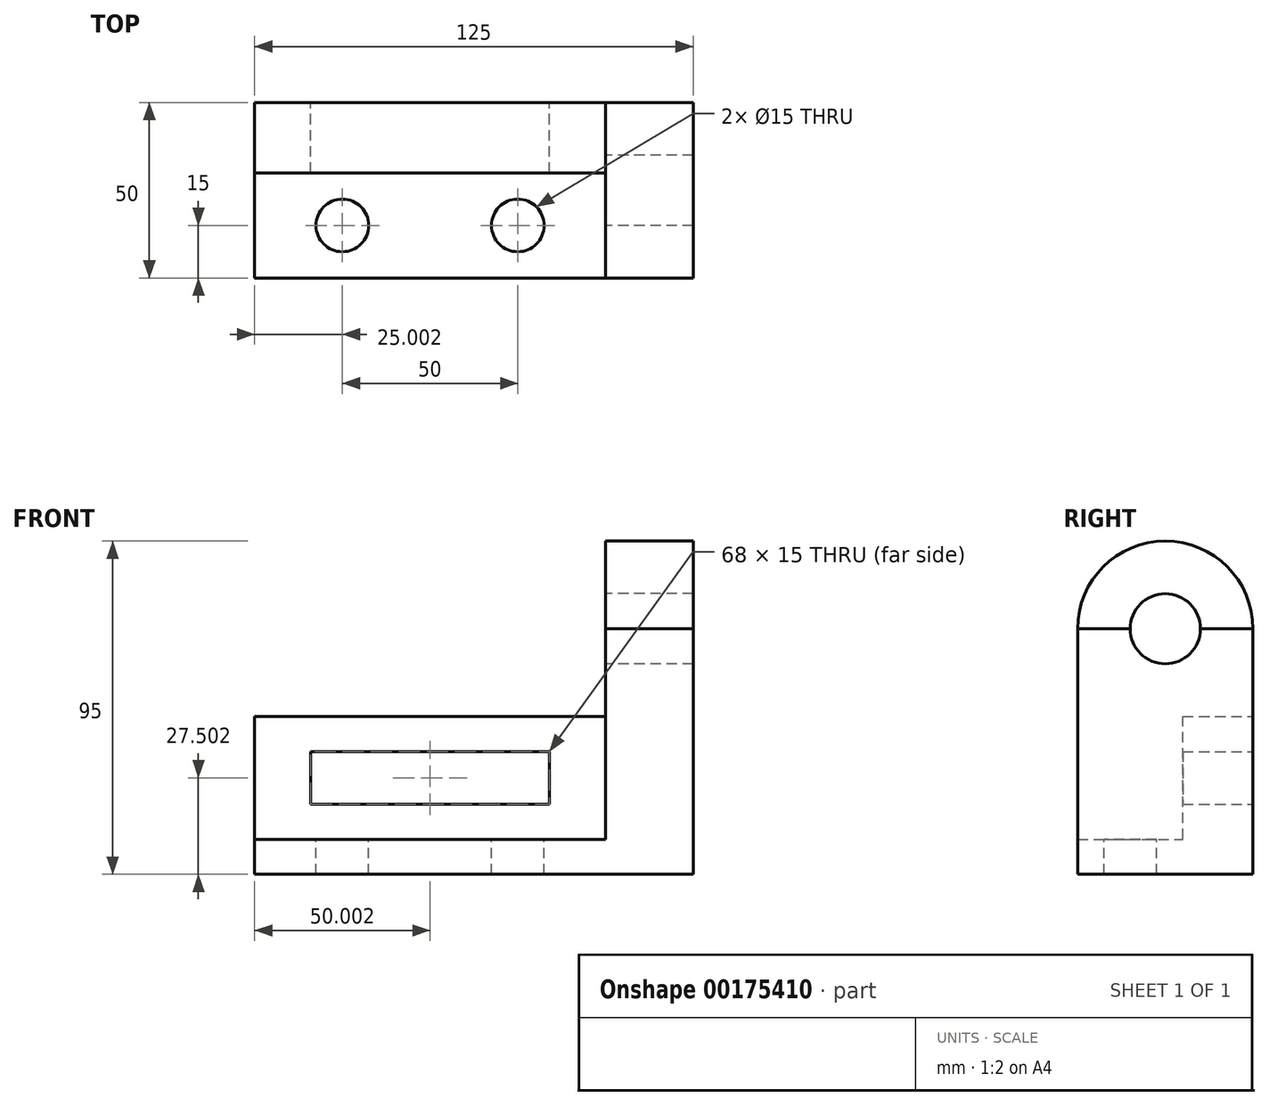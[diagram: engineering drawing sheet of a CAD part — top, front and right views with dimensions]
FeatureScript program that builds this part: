
annotation { "Feature Type Name" : "Feature", "Feature Type Description" : "" }
export const myFeature = defineFeature(function(context is Context, id is Id, definition is map)
    precondition{}
    {
        {
            var Q0;
            Q0=qCreatedBy(makeId("Front.planeOp"),FACE);
            var sketch = newSketch(context, id + "F0", { "sketchPlane" : qUnion([Q0])});
            skLineSegment(sketch, "E0.right", {"start": v(-50, 4.52) * mm, "end": v(-50, -5.48) * mm});
            skPoint(sketch, "E0.middle", {"position": v(0, 0) * mm});
            skLineSegment(sketch, "E1", {"start": v(-50, -5.48) * mm, "end": v(75, -5.48) * mm});
            skLineSegment(sketch, "E2", {"start": v(75, -5.48) * mm, "end": v(75, 64.52) * mm});
            skLineSegment(sketch, "E3", {"start": v(-50, 4.52) * mm, "end": v(50, 4.52) * mm});
            skLineSegment(sketch, "E4", {"start": v(50, 4.52) * mm, "end": v(50, 64.52) * mm});
            skLineSegment(sketch, "E5", {"start": v(-50, 4.52) * mm, "end": v(-50, 39.52) * mm});
            skLineSegment(sketch, "E6", {"start": v(-50, 39.52) * mm, "end": v(50, 39.52) * mm});
            skLineSegment(sketch, "E7", {"start": v(-34, 29.52) * mm, "end": v(34, 29.52) * mm});
            skLineSegment(sketch, "E8", {"start": v(-34, 29.52) * mm, "end": v(-34, 14.52) * mm});
            skLineSegment(sketch, "E9", {"start": v(34, 29.52) * mm, "end": v(34, 14.52) * mm});
            skLineSegment(sketch, "E10", {"start": v(-34, 14.52) * mm, "end": v(34, 14.52) * mm});
            skLineSegment(sketch, "E11", {"start": v(50, 64.52) * mm, "end": v(75, 64.52) * mm});
            skSolve(sketch);
        }
        {
            var Q0;
            Q0 = qSketchRegion(id + "F0", true);
            extrude(context, id + "F1", {"entities" : qUnion([Q0]), "depth" : 50 * mm});
        }
        {
            var Q0;
            Q0=makeQuery(id+"F1.opExtrude","SWEPT_FACE",FACE,{"disambiguationData":[OSD([sQuery(id+"F0.wireOp",EDGE,"E6")])]});
            var sketch = newSketch(context, id + "F2", { "sketchPlane" : qUnion([Q0])});
            skLineSegment(sketch, "E12", {"start": v(-50, 0) * mm, "end": v(-50, -20) * mm});
            skLineSegment(sketch, "E13", {"start": v(-50, -20) * mm, "end": v(50, -20) * mm});
            skLineSegment(sketch, "E14", {"start": v(50, -20) * mm, "end": v(50, 0) * mm});
            skLineSegment(sketch, "E15", {"start": v(50, 0) * mm, "end": v(-50, 0) * mm});
            skSolve(sketch);
        }
        {
            var Q0;
            {var subQ0=sQuery(id+"F2.wireOp",EDGE,"E13");Q0=makeQuery(id+"F2.imprint","IMPRINT",FACE,{"disambiguationData":[TD([[makeQuery(id+"F2.imprint","IMPRINT",EDGE,{"derivedFrom":subQ0}),-1.0]])]});}
            var sketch = newSketch(context, id + "F3", { "sketchPlane" : qUnion([Q0])});
            skSolve(sketch);
        }
        {
            var Q0;
            Q0 = qSketchRegion(id + "F3", true);
            var Q1;
            {var subQ0=sQuery(id+"F2.wireOp",EDGE,"E13");Q1=makeQuery(id+"F2.imprint","IMPRINT",FACE,{"disambiguationData":[TD([[makeQuery(id+"F2.imprint","IMPRINT",EDGE,{"derivedFrom":subQ0}),-1.0]])]});}
            extrude(context, id + "F4", {"entities" : qUnion([Q0, Q1]), "operationType" : NewBodyOperationType.REMOVE, "oppositeDirection" : true, "depth" : 35 * mm});
        }
        {
            var Q0;
            Q0=makeQuery(id+"F4.boolean.opBoolean","COPY",FACE,{"derivedFrom":makeQuery(id+"F4.opExtrude","CAP_FACE",FACE,{"disambiguationData":[OSD([sQuery(id+"F0.wireOp",EDGE,"E4"),sQuery(id+"F0.wireOp",EDGE,"E5"),sQuery(id+"F0.wireOp",EDGE,"E6"),sQuery(id+"F2.wireOp",EDGE,"E13")])],"isStart":false})});
            var sketch = newSketch(context, id + "F5", { "sketchPlane" : qUnion([Q0])});
            skLineSegment(sketch, "E16", {"start": v(-25, -20) * mm, "end": v(-50, -20) * mm});
            skLineSegment(sketch, "E17", {"start": v(25, -20) * mm, "end": v(50, -20) * mm});
            skLineSegment(sketch, "E18", {"start": v(50, -20) * mm, "end": v(50, -35) * mm});
            skLineSegment(sketch, "E19", {"start": v(50, -35) * mm, "end": v(50, -20) * mm});
            skCircle(sketch, "E20", {"center": v(-25, -35) * mm, "radius": 7.5 * mm});
            skCircle(sketch, "E21", {"center": v(25, -35) * mm, "radius": 7.5 * mm});
            skSolve(sketch);
        }
        {
            var Q0;
            Q0 = qSketchRegion(id + "F5", true);
            extrude(context, id + "F6", {"entities" : qUnion([Q0]), "operationType" : NewBodyOperationType.REMOVE, "oppositeDirection" : true, "depth" : 2540 * mm});
        }
        {
            var Q0;
            Q0=makeQuery(id+"F1.opExtrude","SWEPT_FACE",FACE,{"disambiguationData":[OSD([sQuery(id+"F0.wireOp",EDGE,"E2")])]});
            var sketch = newSketch(context, id + "F7", { "sketchPlane" : qUnion([Q0])});
            skArc(sketch, "E22", {"start": v(0, 64.52) * mm, "mid": v(-25, 89.52) * mm, "end": v(-50, 64.52) * mm});
            skSolve(sketch);
        }
        {
            var Q0;
            Q0=makeQuery(id+"F7.imprint","IMPRINT",FACE,{"disambiguationData":[TD([[makeQuery(id+"F7.imprint","IMPRINT",EDGE,{"derivedFrom":sQuery(id+"F7.wireOp",EDGE,"E22")}),1.0]])]});
            extrude(context, id + "F8", {"entities" : qUnion([Q0]), "oppositeDirection" : true, "depth" : 25 * mm});
        }
        {
            var Q0;
            {var subQ0=sQuery(id+"F0.wireOp",EDGE,"E4");Q0=makeQuery(id+"F4.boolean.opBoolean","MERGE",FACE,{"derivedFrom":[makeQuery(id+"F1.opExtrude","SWEPT_FACE",FACE,{"disambiguationData":[OSD([subQ0])]}),makeQuery(id+"F4.opExtrude","SWEPT_FACE",FACE,{"disambiguationData":[OSD([subQ0,sQuery(id+"F0.wireOp",EDGE,"E6")])]})]});}
            var sketch = newSketch(context, id + "F9", { "sketchPlane" : qUnion([Q0])});
            skCircle(sketch, "E23", {"center": v(25, 64.52) * mm, "radius": 10 * mm});
            skSolve(sketch);
        }
        {
            var Q0;
            {var subQ0=sQuery(id+"F9.wireOp",EDGE,"E23");var subQ1=makeQuery(id+"F1.opExtrude","SWEPT_EDGE",EDGE,{"disambiguationData":[OSD([sQuery(id+"F0.wireOp",EDGE,"E4"),sQuery(id+"F0.wireOp",EDGE,"E11")])]});var subQ2=makeQuery(id+"F9.imprint","INTERSECT",VERTEX,{"disambiguationData":[OD(0.0)],"derivedFrom":[subQ1,subQ0]});Q0=makeQuery(id+"F9.imprint","IMPRINT",FACE,{"disambiguationData":[TD([[makeQuery(id+"F9.imprint","IMPRINT",EDGE,{"disambiguationData":[TD([[subQ2,-1.0]])],"derivedFrom":subQ0}),1.0]])]});}
            var Q1;
            {var subQ0=sQuery(id+"F9.wireOp",EDGE,"E23");var subQ1=makeQuery(id+"F1.opExtrude","SWEPT_EDGE",EDGE,{"disambiguationData":[OSD([sQuery(id+"F0.wireOp",EDGE,"E4"),sQuery(id+"F0.wireOp",EDGE,"E11")])]});var subQ2=makeQuery(id+"F9.imprint","INTERSECT",VERTEX,{"disambiguationData":[OD(0.0)],"derivedFrom":[subQ1,subQ0]});Q1=makeQuery(id+"F9.imprint","IMPRINT",FACE,{"disambiguationData":[TD([[makeQuery(id+"F9.imprint","IMPRINT",EDGE,{"disambiguationData":[TD([[subQ2,1.0]])],"derivedFrom":subQ0}),1.0]])]});}
            extrude(context, id + "F10", {"entities" : qUnion([Q0, Q1]), "operationType" : NewBodyOperationType.REMOVE, "oppositeDirection" : true, "depth" : 508 * mm});
        }
        {
            var Q0;
            Q0=makeQuery(id+"F8.opExtrude","CAP_FACE",FACE,{"disambiguationData":[OSD([sQuery(id+"F0.wireOp",EDGE,"E2"),sQuery(id+"F0.wireOp",EDGE,"E11"),sQuery(id+"F7.wireOp",EDGE,"E22")])],"isStart":false});
            var sketch = newSketch(context, id + "F11", { "sketchPlane" : qUnion([Q0])});
            skCircle(sketch, "E24", {"center": v(25, 64.52) * mm, "radius": 10 * mm});
            skSolve(sketch);
        }
        {
            var Q0;
            {var subQ0=sQuery(id+"F11.wireOp",EDGE,"E24");var subQ1=makeQuery(id+"F8.opExtrude","CAP_EDGE",EDGE,{"disambiguationData":[OSD([sQuery(id+"F0.wireOp",EDGE,"E2"),sQuery(id+"F0.wireOp",EDGE,"E11")])],"isStart":false});var subQ2=makeQuery(id+"F11.imprint","INTERSECT",VERTEX,{"disambiguationData":[OD(0.0)],"derivedFrom":[subQ1,subQ0]});Q0=makeQuery(id+"F11.imprint","IMPRINT",FACE,{"disambiguationData":[TD([[makeQuery(id+"F11.imprint","IMPRINT",EDGE,{"disambiguationData":[TD([[subQ2,1.0]])],"derivedFrom":subQ0}),1.0]])]});}
            extrude(context, id + "F12", {"entities" : qUnion([Q0]), "operationType" : NewBodyOperationType.REMOVE, "oppositeDirection" : true, "depth" : 508 * mm});
        }
    });
